# Revit family: FU_Chair_Sandler_Timber 1-2
name_source: partatom
category: Furniture
units: mm (PartAtom-declared; Revit-internal decimal feet)

## family parameters
Always vertical = Yes
Cut with Voids When Loaded = No
OmniClass Number = 23.40.20.00
OmniClass Title = General Furniture and Specialties
Room Calculation Point = No
Shared = No
Work Plane-Based = No

## types (2) — shared parameters
Depth = 520 mm  [stored 1.70604 ft]
Frame = Wood - Beech - Walnut - V
Height = 795 mm  [stored 2.60827 ft]
Manufacturer = Sandler
URL = https://www.sandlerseating.com
Upholstery = Leather - Sandler 134
Width = 510 mm  [stored 1.67323 ft]
zero-valued in all types: Default Elevation

## per-type parameters (varying)
| type | Description | Uph_IsVisible |
| Timber 1.2 | Side chair with an upholstered seat and wooden back on a solid beech frame. | Yes |
| Timber 1.1 | Side chair with solid beech seat, back and frame. | No |

note: column(s) folded — value = type name in every type: Model

note: [stored X ft] marks values corroborated as IEEE doubles in the binary element streams (Revit-internal decimal feet)

## geometry (parser evidence)
native form markers: Sweep x3
no freeform markers — native parametric forms only
